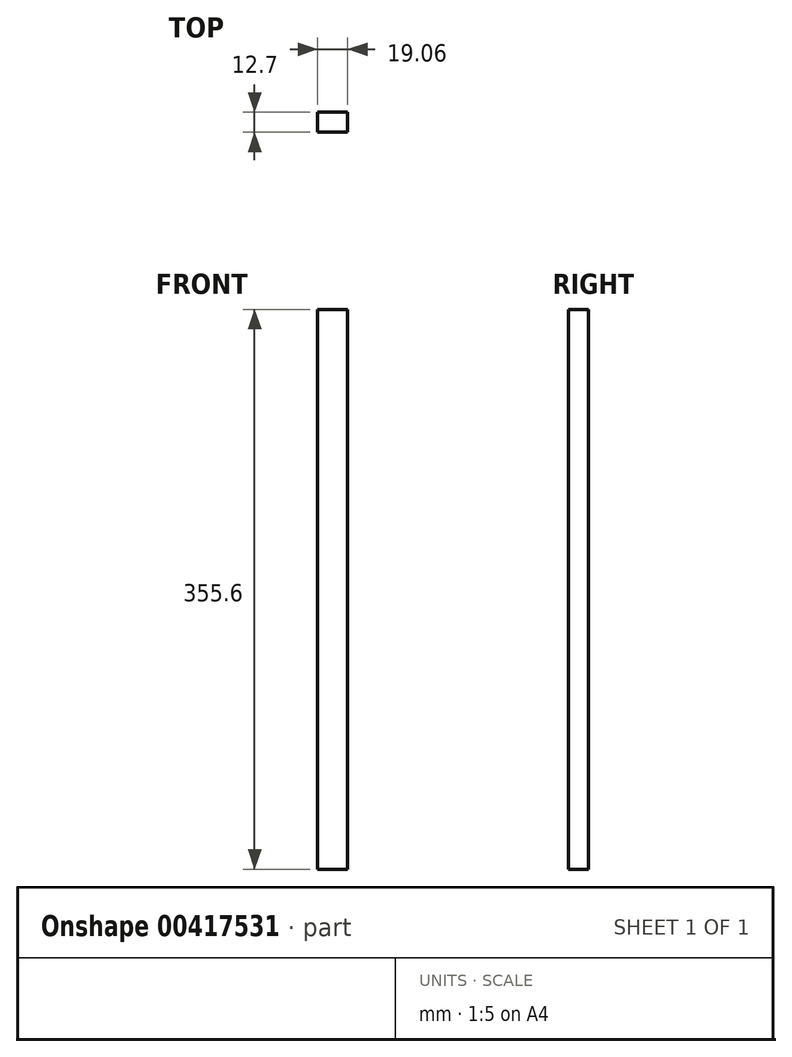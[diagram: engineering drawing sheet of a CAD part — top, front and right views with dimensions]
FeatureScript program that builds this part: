
annotation { "Feature Type Name" : "Feature", "Feature Type Description" : "" }
export const myFeature = defineFeature(function(context is Context, id is Id, definition is map)
    precondition{}
    {
        {
            var Q0;
            Q0=qCreatedBy(makeId("Front.planeOp"),FACE);
            var sketch = newSketch(context, id + "F0", { "sketchPlane" : qUnion([Q0])});
            skLineSegment(sketch, "E0.bottom", {"start": v(-9.52, 177.8) * mm, "end": v(9.53, 177.8) * mm});
            skLineSegment(sketch, "E0.top", {"start": v(-9.53, -177.8) * mm, "end": v(9.52, -177.8) * mm});
            skLineSegment(sketch, "E0.left", {"start": v(-9.52, 177.8) * mm, "end": v(-9.53, -177.8) * mm});
            skLineSegment(sketch, "E0.right", {"start": v(9.53, 177.8) * mm, "end": v(9.52, -177.8) * mm});
            skPoint(sketch, "E0.middle", {"position": v(0, 0) * mm});
            skSolve(sketch);
        }
        {
            var Q0;
            Q0=qSketchRegion(id+"F0",true);
            extrude(context, id + "F1", {"entities" : qUnion([Q0]), "depth" : 12.7 * mm});
        }
    });
